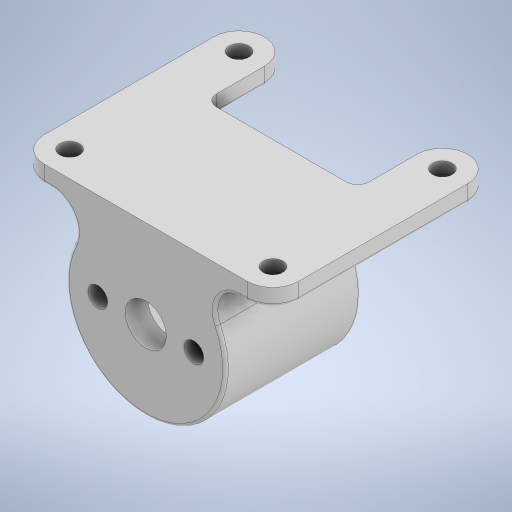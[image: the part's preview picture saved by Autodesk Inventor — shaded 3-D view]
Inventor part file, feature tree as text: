
AUTODESK INVENTOR PART (.ipt)
format: ipt  version: 2024.2 (Build 282272000, 272)  size: 407,552 bytes
history: native  units: mm
features: extrude x6, sketch x6, fillet x3, plane x1
ambient origin geometry x8: Origin, YZ Plane, XZ Plane, XY Plane, X Axis, Y Axis, Z Axis, Center Point
bodies: Solid1 (feature_tree)
feature tree (16):
  extrude  "Extrusion1"  Depth=3.5mm
  extrude  "Extrusion2"  Depth=28.2mm
  plane  "Work Plane1"
  extrude  "Extrusion6"  Depth=25.2mm
  extrude  "Extrusion7"  Depth=12.6mm
  fillet  "Fillet3"  Radius=45.0mm
  extrude  "Extrusion8"  Depth=3.5mm
  fillet  "Fillet4"  Radius=4.5mm
  fillet  "Fillet5"  Radius=4.5mm
  extrude  "Extrusion5"  Depth=5.25mm
  sketch  "Sketch1"  dims[d0=7.25mm d1=3.5mm]
  sketch  "Sketch2"  dims[d2=17.0mm d3=28.2mm]
  sketch  "Sketch3"  dims[d4=4.0mm d5=0.0mm d6=25.2mm]
  sketch  "Sketch5"  dims[d7=20.0mm d8=0.0mm d13=12.6mm d14=45.0mm]
  sketch  "Sketch6"  dims[d15=22.5mm d16=3.5mm d17=4.5mm d18=4.5mm]
  sketch  "Sketch7"  dims[d19=4.5mm d28=5.25mm d29=2.0mm d30=0.0mm d31=30.0mm d44=3.0mm d45=0.0mm d46=5.25mm d47=1.0mm d48=0.0mm d49=4.5mm d50=1.0mm d51=0.0mm d52=2.0mm d53=0.5mm d42=0.5mm d43=0.872665mm]
